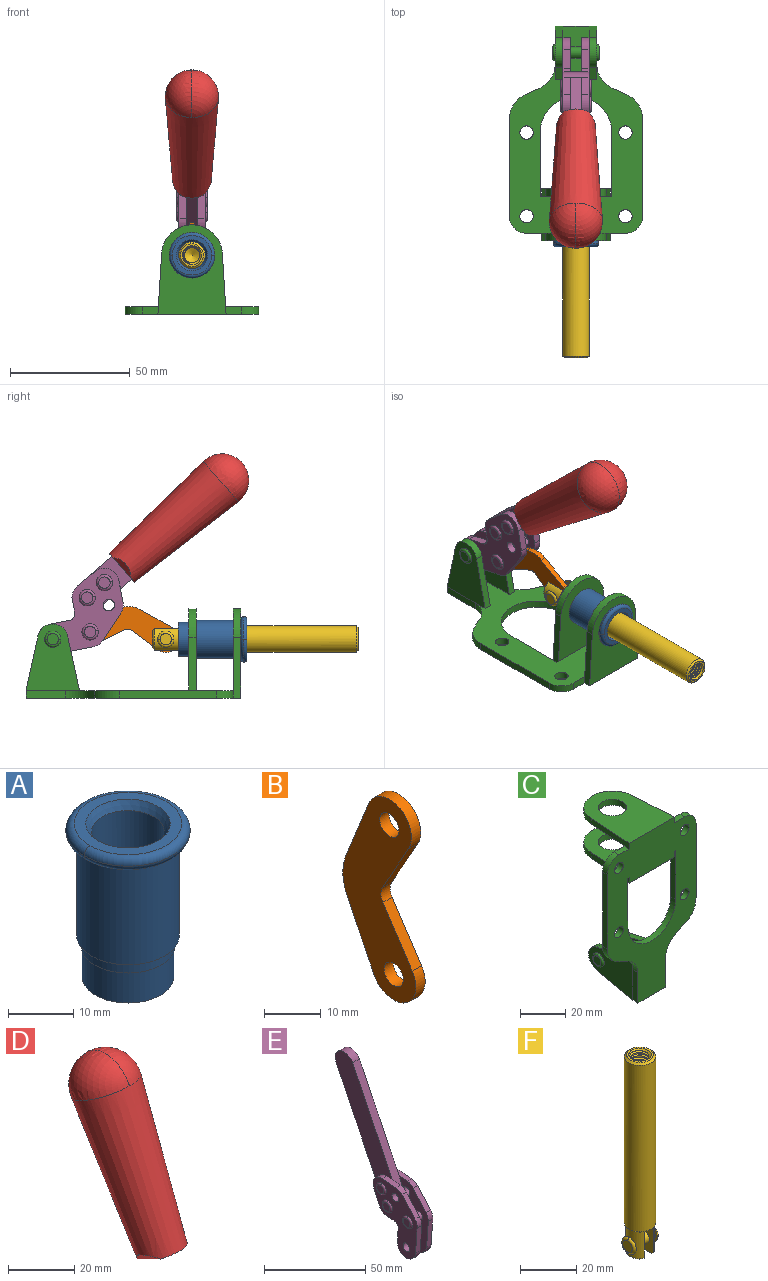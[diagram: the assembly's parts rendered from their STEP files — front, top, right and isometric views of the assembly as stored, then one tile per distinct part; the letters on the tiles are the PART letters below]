
ASSEMBLY  parts=6 mates=6
PART A: 15 faces, bbox 20.6x20.6x28.7 mm
  f0: torus R=8.26mm, axis (0,0,1), area 56.8mm2, adj f1,f10,f12
  f1: torus R=8.26mm, axis (0,0,1), area 56.8mm2, adj f0,f6,f13
  f2: cylinder r=5.59mm len=25.91mm, axis (0,0,1), area 909.6mm2, adj f3,f4
  f3: cone r=6.86mm half-angle=45deg, axis (0,0,-1), area 70.2mm2, adj f2,f14
  f4: cone r=6.47mm half-angle=30deg, axis (0,0,1), area 66.7mm2, adj f2,f13
  f5: cylinder r=7.04mm len=14.07mm, axis (0,0,1), area 252.6mm2, adj f11,f14
  f6: torus R=8.26mm, axis (0,0,1), area 56.8mm2, adj f1,f12,f13
  f7: cylinder r=7.16mm len=14.33mm, axis (0,0,1), area 91.5mm2, adj f9,f11
  f8: cylinder r=7.86mm len=18.42mm, axis (0,0,1), area 909.6mm2, adj f9,f10
  f9: plane 15.72x15.72mm, normal (0,0,-1), area 33mm2, adj f7,f8
  f10: plane 16.51x16.51mm, normal (0,0,-1), area 19.9mm2, adj f0,f8,f12
  f11: plane 14.33x14.33mm, normal (0,0,-1), area 5.7mm2, adj f5,f7
  f12: torus R=8.26mm, axis (0,0,1), area 56.8mm2, adj f0,f6,f10
  f13: plane 16.51x16.51mm, normal (0,0,1), area 82.7mm2, adj f1,f4,f6
  f14: plane 14.07x14.07mm, normal (0,0,-1), area 7.8mm2, adj f3,f5
PART B: 12 faces, bbox 2.3x18.2x42.8 mm
  f0: cylinder r=2.4mm len=4.8mm, axis (1,0,0), area 34.9mm2, adj f4,f11
  f1: cylinder r=10.41mm len=8.47mm, axis (1,0,0), area 20.2mm2, adj f4,f9,f10,f11
  f2: cylinder r=3.05mm len=3.16mm, axis (1,0,0), area 7.7mm2, adj f4,f6,f7,f11
  f3: cylinder r=2.4mm len=4.8mm, axis (1,0,0), area 34.9mm2, adj f4,f11
  f4: plane 42.81x18.23mm, normal (-1,0,0), area 414.1mm2, adj f0,f1,f2,f3,f5,f6,f7,f8
  f5: cylinder r=5.54mm len=10.67mm, axis (1,0,0), area 41.8mm2, adj f4,f6,f10,f11
  f6: plane 11.66x6.53mm, normal (0,-0.87,-0.49), area 30.9mm2, adj f2,f4,f5,f11
  f7: plane 11.17x7.33mm, normal (0,-0.84,0.55), area 30.9mm2, adj f2,f4,f8,f11
  f8: cylinder r=5.54mm len=10.51mm, axis (1,0,0), area 41.8mm2, adj f4,f7,f9,f11
  f9: plane 13.67x6.67mm, normal (0,0.9,-0.44), area 35.1mm2, adj f1,f4,f8,f11
  f10: plane 14.1x5.7mm, normal (0,0.93,0.37), area 35.1mm2, adj f1,f4,f5,f11
  f11: plane 42.81x18.23mm, normal (1,0,0), area 414.1mm2, adj f0,f1,f2,f3,f5,f6,f7,f8
PART C: 55 faces, bbox 55.7x37.4x89.8 mm
  f0: torus R=2.41mm, axis (-1,0,0), area 15mm2, adj f11,f15,f25
  f1: torus R=2.41mm, axis (-1,0,0), area 15mm2, adj f10,f12,f22
  f2: cylinder r=2.78mm len=5.56mm, axis (0,-1,0), area 54.2mm2, adj f30,f54
  f3: cylinder r=14.99mm len=29.97mm, axis (0,-1,0), area 145.9mm2, adj f30,f49,f53,f54
  f4: cylinder r=2.78mm len=5.56mm, axis (0,-1,0), area 54.2mm2, adj f30,f54
  f5: cylinder r=2.78mm len=5.56mm, axis (0,-1,0), area 54.2mm2, adj f30,f54
  f6: cylinder r=2.78mm len=5.56mm, axis (0,-1,0), area 54.2mm2, adj f30,f54
  f7: cylinder r=6.35mm len=12.7mm, axis (0,0,1), area 123.6mm2, adj f27,f51
  f8: cylinder r=6.35mm len=12.7mm, axis (0,0,-1), area 124.7mm2, adj f21,f35
  f9: cylinder r=2.41mm len=11.18mm, axis (-1,0,0), area 169.4mm2, adj f16,f19
  f10: plane 4.83x4.83mm, normal (1,0,0), area 18.3mm2, adj f1,f12
  f11: plane 4.83x4.83mm, normal (-1,0,0), area 18.3mm2, adj f0,f15
  f12: torus R=2.41mm, axis (-1,0,0), area 15mm2, adj f1,f10,f22
  f13: cylinder r=6.35mm len=12.41mm, axis (1,0,0), area 53.4mm2, adj f18,f19,f22,f23
  f14: cylinder r=6.35mm len=12.41mm, axis (-1,0,0), area 53.4mm2, adj f16,f17,f24,f25
  f15: torus R=2.41mm, axis (-1,0,0), area 15mm2, adj f0,f11,f25
  f16: plane 27.86x22.35mm, normal (1,0,0), area 425.4mm2, adj f9,f14,f17,f24,f30
  f17: plane 22.86x4.97mm, normal (0,0.21,0.98), area 72.5mm2, adj f14,f16,f25,f30
  f18: plane 22.86x4.97mm, normal (0,0.21,0.98), area 72.5mm2, adj f13,f19,f22,f30
  f19: plane 27.86x22.35mm, normal (-1,0,0), area 425.4mm2, adj f9,f13,f18,f23,f30
  f20: cylinder r=12.7mm len=25.35mm, axis (0,0,-1), area 119.8mm2, adj f21,f34,f35,f36
  f21: plane 34.21x28.07mm, normal (0,0,-1), area 702.4mm2, adj f8,f20,f30,f34,f36
  f22: plane 27.96x22.45mm, normal (1,0,0), area 407.2mm2, adj f1,f12,f13,f18,f23,f30,f42,f43
  f23: plane 22.86x4.97mm, normal (0,0.21,-0.98), area 72.5mm2, adj f13,f19,f22,f44
  f24: plane 22.86x4.97mm, normal (0,0.21,-0.98), area 72.5mm2, adj f14,f16,f25,f44
  f25: plane 27.86x22.35mm, normal (-1,0,0), area 407.1mm2, adj f0,f14,f15,f17,f24,f30,f45,f46
  f26: plane 3.1x0.95mm, normal (0,0,-1), area 2.7mm2, adj f30,f49,f50,f54
  f27: plane 34.21x28.07mm, normal (0,0,1), area 702.4mm2, adj f7,f28,f30,f50,f52
  f28: cylinder r=12.7mm len=25.35mm, axis (0,0,1), area 118.8mm2, adj f27,f50,f51,f52
  f29: plane 3.1x0.95mm, normal (0,0,-1), area 2.7mm2, adj f30,f52,f53,f54
  f30: plane 86.54x55.63mm, normal (0,1,0), area 2362.9mm2, adj f2,f3,f4,f5,f6,f16,f17,f18
  f31: plane 40.56x3.1mm, normal (-1,0,0), area 125.7mm2, adj f30,f32,f48,f54
  f32: cylinder r=7.11mm len=7.11mm, axis (0,-1,0), area 34.6mm2, adj f30,f31,f33,f54
  f33: plane 6.67x3.1mm, normal (0,0,1), area 20.4mm2, adj f30,f32,f34,f54
  f34: plane 25.39x3.13mm, normal (-1,0.06,0), area 79.5mm2, adj f20,f21,f33,f35,f54
  f35: plane 37.31x28.45mm, normal (0,0,1), area 789.9mm2, adj f8,f20,f34,f36,f54
  f36: plane 25.39x3.13mm, normal (1,0.06,0), area 79.5mm2, adj f20,f21,f35,f37,f54
  f37: plane 6.67x3.1mm, normal (0,0,1), area 20.4mm2, adj f30,f36,f38,f54
  f38: cylinder r=7.11mm len=7.11mm, axis (0,-1,0), area 34.6mm2, adj f30,f37,f39,f54
  f39: plane 40.56x3.1mm, normal (1,0,0), area 125.7mm2, adj f30,f38,f40,f54
  f40: cylinder r=11.18mm len=10.16mm, axis (0,-1,0), area 39.5mm2, adj f30,f39,f41,f54
  f41: plane 6.09x3.1mm, normal (0.42,0,-0.91), area 20.8mm2, adj f30,f40,f42,f54
  f42: cylinder r=11.18mm len=9.41mm, axis (0,-1,0), area 37.2mm2, adj f22,f30,f41,f43,f54
  f43: plane 16.5x3.1mm, normal (1,0,0), area 51.1mm2, adj f22,f42,f44,f54
  f44: plane 17.37x3.1mm, normal (0,0,-1), area 53.8mm2, adj f23,f24,f30,f43,f45,f54
  f45: plane 16.5x3.1mm, normal (-1,0,0), area 51.1mm2, adj f25,f44,f46,f54
  f46: cylinder r=11.18mm len=9.41mm, axis (0,-1,0), area 37.2mm2, adj f25,f30,f45,f47,f54
  f47: plane 6.09x3.1mm, normal (-0.42,0,-0.91), area 20.8mm2, adj f30,f46,f48,f54
  f48: cylinder r=11.18mm len=10.16mm, axis (0,-1,0), area 39.5mm2, adj f30,f31,f47,f54
  f49: plane 26.54x3.1mm, normal (-1,0,0), area 82.3mm2, adj f3,f26,f30,f54
  f50: plane 25.39x3.1mm, normal (1,0.06,0), area 78.8mm2, adj f26,f27,f28,f51,f54
  f51: plane 37.31x28.45mm, normal (0,0,-1), area 789.9mm2, adj f7,f28,f50,f52,f54
  f52: plane 25.39x3.1mm, normal (-1,0.06,0), area 78.8mm2, adj f27,f28,f29,f51,f54
  f53: plane 26.54x3.1mm, normal (1,0,0), area 82.3mm2, adj f3,f29,f30,f54
  f54: plane 89.66x55.63mm, normal (0,-1,0), area 2678.5mm2, adj f2,f3,f4,f5,f6,f26,f29,f31
PART D: 11 faces, bbox 22.3x42.6x64.5 mm
  f0: sphere r=11.13mm, area 411.4mm2, adj f1,f8
  f1: cone r=11.11mm half-angle=3.3deg, axis (0,0.44,0.9), area 3251.8mm2, adj f0,f7,f8,f9,f10
  f2: cylinder r=6.16mm len=11.7mm, axis (1,0,0), area 89.5mm2, adj f3,f4,f5,f6
  f3: plane 60.23x36.75mm, normal (-1,0,0), area 763.6mm2, adj f2,f4,f6,f10
  f4: plane 51.37x25.05mm, normal (0,0.9,-0.44), area 264.2mm2, adj f2,f3,f5,f10
  f5: plane 60.23x36.75mm, normal (1,0,0), area 763.6mm2, adj f2,f4,f6,f10
  f6: plane 51.37x25.05mm, normal (0,-0.9,0.44), area 264.2mm2, adj f2,f3,f5,f10
  f7: plane 9.95x5.95mm, normal (0.71,-0.31,-0.64), area 25.8mm2, adj f1,f10
  f8: sphere r=11.13mm, area 411.4mm2, adj f0,f1
  f9: plane 9.95x5.95mm, normal (-0.71,-0.31,-0.64), area 25.8mm2, adj f1,f10
  f10: plane 14.27x11.38mm, normal (0,-0.44,-0.9), area 106.7mm2, adj f1,f3,f4,f5,f6,f7,f9
PART E: 59 faces, bbox 12.9x60.2x99.6 mm
  f0: torus R=2.39mm, axis (-1,0,0), area 14.9mm2, adj f20,f43,f51
  f1: torus R=2.39mm, axis (-1,0,0), area 14.9mm2, adj f19,f42,f51
  f2: torus R=2.39mm, axis (-1,0,0), area 14.9mm2, adj f18,f35,f51
  f3: torus R=2.39mm, axis (-1,0,0), area 14.9mm2, adj f14,f17,f23
  f4: torus R=2.39mm, axis (-1,0,0), area 14.9mm2, adj f13,f16,f23
  f5: torus R=2.39mm, axis (-1,0,0), area 14.9mm2, adj f12,f15,f23
  f6: cylinder r=2.39mm len=4.78mm, axis (1,0,0), area 46.5mm2, adj f48,f50,f51
  f7: cylinder r=2.39mm len=4.78mm, axis (1,0,0), area 46.5mm2, adj f50,f51
  f8: cylinder r=6.35mm len=12.68mm, axis (1,0,0), area 61.8mm2, adj f38,f39,f50,f51
  f9: cylinder r=2.39mm len=4.78mm, axis (-1,0,0), area 70.5mm2, adj f46,f50
  f10: cylinder r=2.39mm len=4.78mm, axis (-1,0,0), area 46.5mm2, adj f23,f45,f46
  f11: cylinder r=2.39mm len=4.78mm, axis (-1,0,0), area 46.5mm2, adj f23,f46
  f12: plane 4.78x4.78mm, normal (1,0,0), area 17.9mm2, adj f5,f15
  f13: plane 4.78x4.78mm, normal (1,0,0), area 17.9mm2, adj f4,f16
  f14: plane 4.78x4.78mm, normal (1,0,0), area 17.9mm2, adj f3,f17
  f15: torus R=2.39mm, axis (-1,0,0), area 14.9mm2, adj f5,f12,f23
  f16: torus R=2.39mm, axis (-1,0,0), area 14.9mm2, adj f4,f13,f23
  f17: torus R=2.39mm, axis (-1,0,0), area 14.9mm2, adj f3,f14,f23
  f18: plane 4.78x4.78mm, normal (-1,0,0), area 17.9mm2, adj f2,f35
  f19: plane 4.78x4.78mm, normal (-1,0,0), area 17.9mm2, adj f1,f42
  f20: plane 4.78x4.78mm, normal (-1,0,0), area 17.9mm2, adj f0,f43
  f21: plane 2.26x0.2mm, normal (1,0,0), area 0.2mm2, adj f31,f44
  f22: plane 2.26x0.2mm, normal (-1,0,0), area 0.2mm2, adj f41,f44
  f23: plane 39.37x30.77mm, normal (1,0,0), area 565.5mm2, adj f3,f4,f5,f10,f11,f15,f16,f17
  f24: cylinder r=6.1mm len=4.15mm, axis (-1,0,0), area 14.7mm2, adj f23,f25,f32,f46
  f25: plane 10.25x9.01mm, normal (0,-0.75,0.66), area 42.3mm2, adj f23,f24,f26,f46
  f26: cylinder r=6.35mm len=4.64mm, axis (-1,0,0), area 15.6mm2, adj f23,f25,f27,f46
  f27: plane 15.84x3.1mm, normal (0,-1,-0.07), area 49.2mm2, adj f23,f26,f28,f46
  f28: cylinder r=6.35mm len=12.68mm, axis (-1,0,0), area 61.8mm2, adj f23,f27,f29,f46
  f29: plane 8.11x3.1mm, normal (0,1,0.07), area 25.2mm2, adj f23,f28,f30,f46
  f30: cylinder r=3.05mm len=3.25mm, axis (-1,0,0), area 14.8mm2, adj f23,f29,f31,f46
  f31: plane 5.99x3.1mm, normal (0,0.07,-1), area 18.6mm2, adj f21,f23,f30,f44,f46
  f32: plane 9.5x3.1mm, normal (0,-0.07,1), area 29.5mm2, adj f23,f24,f33,f46,f47
  f33: cylinder r=6.1mm len=8.63mm, axis (-1,0,0), area 39.1mm2, adj f23,f32,f34,f47
  f34: plane 8.65x3.96mm, normal (0,0.91,-0.42), area 29.5mm2, adj f23,f33,f44,f47
  f35: torus R=2.39mm, axis (-1,0,0), area 14.9mm2, adj f2,f18,f51
  f36: plane 10.25x9.01mm, normal (0,-0.75,0.66), area 42.3mm2, adj f37,f49,f50,f51
  f37: cylinder r=6.35mm len=4.64mm, axis (1,0,0), area 15.6mm2, adj f36,f38,f50,f51
  f38: plane 15.84x3.1mm, normal (0,-1,-0.07), area 49.2mm2, adj f8,f37,f50,f51
  f39: plane 8.11x3.1mm, normal (0,1,0.07), area 25.2mm2, adj f8,f40,f50,f51
  f40: cylinder r=3.05mm len=3.25mm, axis (1,0,0), area 14.8mm2, adj f39,f41,f50,f51
  f41: plane 5.99x3.1mm, normal (0,0.07,-1), area 18.6mm2, adj f22,f40,f44,f50,f51
  f42: torus R=2.39mm, axis (-1,0,0), area 14.9mm2, adj f1,f19,f51
  f43: torus R=2.39mm, axis (-1,0,0), area 14.9mm2, adj f0,f20,f51
  f44: cylinder r=6.35mm len=12.12mm, axis (-1,0,0), area 128.9mm2, adj f21,f22,f23,f31,f34,f41,f46,f47
  f45: plane 2.65x1.35mm, normal (1,0,0), area 1mm2, adj f10,f55
  f46: plane 39.08x20.42mm, normal (-1,0,0), area 412.5mm2, adj f9,f10,f11,f24,f25,f26,f27,f28
  f47: plane 77.62x39.82mm, normal (1,0,0), area 850mm2, adj f32,f33,f34,f44,f53,f54,f55
  f48: plane 2.65x1.35mm, normal (-1,0,0), area 1mm2, adj f6,f55
  f49: cylinder r=6.1mm len=4.15mm, axis (1,0,0), area 14.7mm2, adj f36,f50,f51,f56
  f50: plane 39.08x20.42mm, normal (1,0,0), area 412.5mm2, adj f6,f7,f8,f9,f36,f37,f38,f39
  f51: plane 39.37x30.77mm, normal (-1,0,0), area 565.5mm2, adj f0,f1,f2,f6,f7,f8,f35,f36
  f52: plane 8.65x3.96mm, normal (0,0.91,-0.42), area 29.5mm2, adj f44,f51,f57,f58
  f53: plane 68.49x33.4mm, normal (0,0.9,-0.44), area 358.1mm2, adj f44,f47,f54,f58
  f54: cylinder r=6.35mm len=12.06mm, axis (1,0,0), area 93.7mm2, adj f47,f53,f55,f58
  f55: plane 68.49x33.4mm, normal (0,-0.9,0.44), area 358.1mm2, adj f44,f45,f46,f47,f48,f50,f54,f58
  f56: plane 9.5x3.1mm, normal (0,-0.07,1), area 29.5mm2, adj f49,f50,f51,f57,f58
  f57: cylinder r=6.1mm len=8.63mm, axis (1,0,0), area 39.1mm2, adj f51,f52,f56,f58
  f58: plane 77.62x39.82mm, normal (-1,0,0), area 850mm2, adj f44,f52,f53,f54,f55,f56,f57
PART F: 48 faces, bbox 12.6x11.1x86.1 mm
  f0: torus R=2.41mm, axis (-1,0,0), area 15mm2, adj f30,f32,f34
  f1: torus R=2.41mm, axis (-1,0,0), area 15mm2, adj f29,f31,f33
  f2: cylinder r=5.54mm len=72.39mm, axis (0,0,1), area 2518.5mm2, adj f3,f4,f42,f43
  f3: cone r=5.54mm half-angle=45deg, axis (0,0,1), area 7.6mm2, adj f2,f5,f41
  f4: cone r=5.54mm half-angle=45deg, axis (0,0,-1), area 34.9mm2, adj f2,f39
  f5: cylinder r=5.08mm len=11.48mm, axis (0,0,1), area 108.3mm2, adj f3,f7,f8,f41
  f6: cylinder r=2.41mm len=4.83mm, axis (-1,0,0), area 71.2mm2, adj f40,f41
  f7: cylinder r=2.41mm len=4.83mm, axis (-1,0,0), area 7.6mm2, adj f5,f34
  f8: cone r=5.08mm half-angle=45deg, axis (0,0,1), area 10.6mm2, adj f5,f37,f41
  f9: cone r=3.98mm half-angle=45deg, axis (0,0,1), area 17.6mm2, adj f27,f39,f45,f46,f47
  f10: cylinder r=2.41mm len=4.83mm, axis (-1,0,0), area 7.6mm2, adj f33,f38
  f11: cylinder r=3.2mm len=6.4mm, axis (0,0,1), area 78.4mm2, adj f12,f28,f44,f45,f47
  f12: cylinder r=3.2mm len=6.4mm, axis (0,0,1), area 10.5mm2, adj f11,f13,f45,f47
  f13: cylinder r=3.2mm len=6.4mm, axis (0,0,1), area 10.5mm2, adj f12,f14,f45,f47
  f14: cylinder r=3.2mm len=6.4mm, axis (0,0,1), area 10.5mm2, adj f13,f15,f45,f47
  f15: cylinder r=3.2mm len=6.4mm, axis (0,0,1), area 10.5mm2, adj f14,f16,f45,f47
  f16: cylinder r=3.2mm len=6.4mm, axis (0,0,1), area 10.5mm2, adj f15,f17,f45,f47
  f17: cylinder r=3.2mm len=6.4mm, axis (0,0,1), area 10.5mm2, adj f16,f18,f45,f47
  f18: cylinder r=3.2mm len=6.4mm, axis (0,0,1), area 10.5mm2, adj f17,f19,f45,f47
  f19: cylinder r=3.2mm len=6.4mm, axis (0,0,1), area 10.5mm2, adj f18,f20,f45,f47
  f20: cylinder r=3.2mm len=6.4mm, axis (0,0,1), area 10.5mm2, adj f19,f21,f45,f47
  f21: cylinder r=3.2mm len=6.4mm, axis (0,0,1), area 10.5mm2, adj f20,f22,f45,f47
  f22: cylinder r=3.2mm len=6.4mm, axis (0,0,1), area 10.5mm2, adj f21,f23,f45,f47
  f23: cylinder r=3.2mm len=6.4mm, axis (0,0,1), area 10.5mm2, adj f22,f24,f45,f47
  f24: cylinder r=3.2mm len=6.4mm, axis (0,0,1), area 10.5mm2, adj f23,f25,f45,f47
  f25: cylinder r=3.2mm len=6.4mm, axis (0,0,1), area 10.5mm2, adj f24,f26,f45,f47
  f26: cylinder r=3.2mm len=6.4mm, axis (0,0,1), area 10.5mm2, adj f25,f27,f45,f47
  f27: cylinder r=3.2mm len=6.4mm, axis (0,0,1), area 7.4mm2, adj f9,f26,f45,f47
  f28: cone r=3.2mm half-angle=60deg, axis (0,0,1), area 37.2mm2, adj f11
  f29: plane 4.83x4.83mm, normal (-1,0,0), area 18.3mm2, adj f1,f31
  f30: plane 4.83x4.83mm, normal (1,0,0), area 18.3mm2, adj f0,f32
  f31: torus R=2.41mm, axis (-1,0,0), area 15mm2, adj f1,f29,f33
  f32: torus R=2.41mm, axis (-1,0,0), area 15mm2, adj f0,f30,f34
  f33: plane 6.83x6.83mm, normal (1,0,0), area 18.3mm2, adj f1,f10,f31
  f34: plane 6.83x6.83mm, normal (-1,0,0), area 18.3mm2, adj f0,f7,f32
  f35: cone r=5.08mm half-angle=45deg, axis (0,0,1), area 10.6mm2, adj f36,f38,f40
  f36: plane 7.25x1.97mm, normal (0,0,-1), area 10mm2, adj f35,f40
  f37: plane 7.25x1.97mm, normal (0,0,-1), area 10mm2, adj f8,f41
  f38: cylinder r=5.08mm len=11.48mm, axis (0,0,1), area 108.3mm2, adj f10,f35,f40,f42
  f39: plane 9.55x9.55mm, normal (0,0,1), area 22mm2, adj f4,f9
  f40: plane 12.76x10.09mm, normal (1,0,0), area 95.7mm2, adj f6,f35,f36,f38,f42,f43
  f41: plane 12.76x10.09mm, normal (-1,0,0), area 95.7mm2, adj f3,f5,f6,f8,f37,f43
  f42: cone r=5.54mm half-angle=45deg, axis (0,0,1), area 7.6mm2, adj f2,f38,f40
  f43: plane 11.07x4.7mm, normal (0,0,-1), area 50.4mm2, adj f2,f40,f41
  f44: plane 0.89x0.62mm, normal (-1,0,0), area 0.3mm2, adj f11,f45,f46,f47
  f45: bspline ~24.8x7.63mm, area 266.6mm2, adj f9,f11,f12,f13,f14,f15,f16,f17
  f46: bspline ~24.87x7.63mm, area 73.6mm2, adj f9,f44,f45,f47
  f47: bspline ~24.98x7.63mm, area 272.5mm2, adj f9,f11,f12,f13,f14,f15,f16,f17
PLACE A rot(axis=(1,0,0),90deg) t=(0,9.43,0)mm
PLACE B rot(axis=(1,0,0),97.5deg) t=(0,12.88,2.22)mm
PLACE C rot(axis=(1,0,0),90deg) t=(0,9.43,0)mm fixed
PLACE D rot(axis=(1,0,0),75deg) t=(-0.04,4.15,9.14)mm
PLACE E rot(axis=(1,0,0),75deg) t=(0,4.15,9.14)mm
PLACE F rot(axis=(1,0,0),90deg) t=(0,9.81,0)mm
MATE revolute E.f7 <-> C.f0  axis (1,0,0) through (0,41.52,24.61)mm
MATE fastened E.f54 <-> D.f2  axis (-1,0,0) through (-2.35,-30.37,91.94)mm
MATE slider F.f2 <-> A.f2  axis (0,-1,0) through (0,-48.97,24.61)mm
MATE fastened C.f7 <-> A.f2  axis (0,-1,0) through (0,-36.96,24.61)mm
MATE revolute B.f5 <-> F.f6  axis (1,0,0) through (0,-5.67,24.61)mm
MATE revolute B.f3 <-> E.f4  axis (1,0,0) through (0,25.94,27.64)mm
